# Revit family: Drain_Trench-Z874-U-12-HD
name_source: partatom
category: Plumbing Fixtures
units: mm (PartAtom-declared; Revit-internal decimal feet)

## family parameters
Cut with Voids When Loaded = No
Host = Face
OmniClass Number = 23.70.50.21.24
OmniClass Title = Waste Water Drains
Part Type = Normal
Room Calculation Point = No
Round Connector Dimension = Use Radius
Shared = No

## types (1)
- 80 x 12 Wide Throat
    Assembly Code = D2030300
    CW Connection = No
    Cover = Iron - Zurn Industries, LLC - Ductile - Painted Black
    Default Elevation = 4' - 0"
    Description = Utility Trench with Steel Frame, 12 Inch Wide Throat Width and Cover
    Frame = Iron - Zurn Industries, LLC - Ductile - Painted Black
    Frame Depth Specify 4.0 Min to 31.25 Max = 0' - 10"
    HW Connection = No
    Length = 6' - 8"
    Manufacturer = Zurn Industries, LLC
    Model = Z874-U-12-HD
    Product Documentation Link = https://www.zurn.com
    Product Page URL = https://www.zurn.com
    Product data url = https://www.bimobject.com
    Sidewall = Polyethylene - Zurn Industries, LLC - High Density - Grey
    Trench Frame Depth = 0' - 10"
    URL = www.zurn.com
    Vent Connection = No
    Waste Connection = No
    Width = 1' - 5"
    Width of Throat = 1' - 0"

## geometry (parser evidence)
native form markers: Sweep x2
no freeform markers — native parametric forms only
